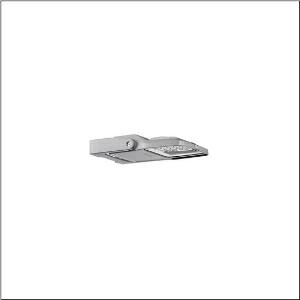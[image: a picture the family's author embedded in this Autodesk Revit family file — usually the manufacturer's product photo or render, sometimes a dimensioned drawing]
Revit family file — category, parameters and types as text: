
# Revit family: floodlight_fl_21_iq_micro___pl33t_5xa7762a2f2a_46b5
name_source: partatom
category: Lighting Fixtures
units: mm (PartAtom-declared; Revit-internal decimal feet)

## family parameters
Cut with Voids When Loaded = No
Host = Face
Light Source = No
Part Type = Normal
Room Calculation Point = No
Round Connector Dimension = Use Diameter
Shared = No

## types (1)
- --- (1 x LED, 2930 lm, 23.1 W, 3000K)
    Apparent Load = 23 VA
    CIE Flux Codes = 26 75 99 100 100
    Color Rendering = 70
    Color Temperature = 3000K
    Default Elevation = 1800 mm
    Description = Floodlight FL 21 iQ micro, floodlight, primary light control with lens, of PMMA, primary optical cover: protective disc, of toughened safety glass, transparent, light distribution: PL33T, light emission: direct distribution, installation type: surface-mounted, lamps: LED, High Power LED, rated values: 2.930lm | 23,1W | 126,8lm/W (begin service life); end service life: 2.930lm | 23,8W; at 50% lumin. flux: 1.465lm | 11W | 133,2lm/W, colour temperature: 3000K, colour rendering: CRI > 70, light colour: 730, light setting 1 begin service life: 100% | 2.930lm | 23,1W | 126,8lm/W | 3.000K, light setting 1 end service life: 23,8W, further light settings possible, control: Auto-Match, Temp-Guard, Night-Set, Smart-Wire, Desk-Remote (wireless, voltage-free reading and setting of iQ features in the workshop via application-optimized NFC function/RFID function), optimised constant luminous flux control (CLO 2.0), Street-Remote, pre-setting: linear dimming characteristic, with terminal, 6-pole, mains connection: 220..240V, AC, 50/60Hz, luminaire housing, of diecast aluminium, powder-coated, SITECO metallic grey (DB 702S), corrosivity category C5 mid according to DIN EN ISO 12944suitable for swimming poolschlorine-resistant, sealing non-destructively replaceable, design bracket, of diecast aluminium, powder-coated, SITECO metallic grey (DB 702S), protection rating (complete): IP66, insulation class (complete): insulation class II (safety insulation), certification: CE, ENEC, VDE, protection symbol: D, impact resistance: IK07, permissible operating ambient temperature: -40..+40°C, permissible operating ambient temperature for outdoor applications: -40..+50°C, standard: DIN EN 12944, LABS conformity tested according to VDMA 24364:2018-05, packaging unit: 1 piece

Light Distribution: PL33T
    Height = 65 mm
    Lamp = 1 x LED
    Lamp Light Flux = 2930 lm
    Lamp Power = 23.1 W
    Lamp count = 1
    Length = 312 mm
    Luminous efficacy = 127 lm/W
    Manufacturer = Siteco
    ModVariant = No
    Model = 5XA7762A2F2A
    Mounting Place = Wall
    Mounting Type = Surface mounted
    Number of Poles = 1
    OnlyDefault = Yes
    Power Factor = 1
    Product Name = Floodlight FL 21 iQ micro | PL33T
    Product group = floodlight | wall mounted
    ProductGroupID = 2002
    Protection Class = Protection class II
    Protection Degree = IP 66
    RLX_Detail_Level = 1
    RLX_Emergency_Light_Flux = 0 lm
    RLX_Emergency_Type = 0
    RLX_Emergency_Type_DB = No
    RlxData = <blob elided: 97601 chars, md5=3d0ffbf2>
    Socket = socket
    Standby Power = 0 W
    System Light Flux = 2930 lm
    System Power = 23 W
    Type Comments = factory setting: luminous flux: 100 % | dim-lin: 254 | 455 mA
    Type Image = l_1006878.jpg
    URL = http://relux.com
    VarID = @adj_149053
    Voltage = 0 V
    Weight = 0.00 kg
    Width = 230 mm

## geometry (parser evidence)
native form markers: Blend x4, Sweep x12
no freeform markers — native parametric forms only
